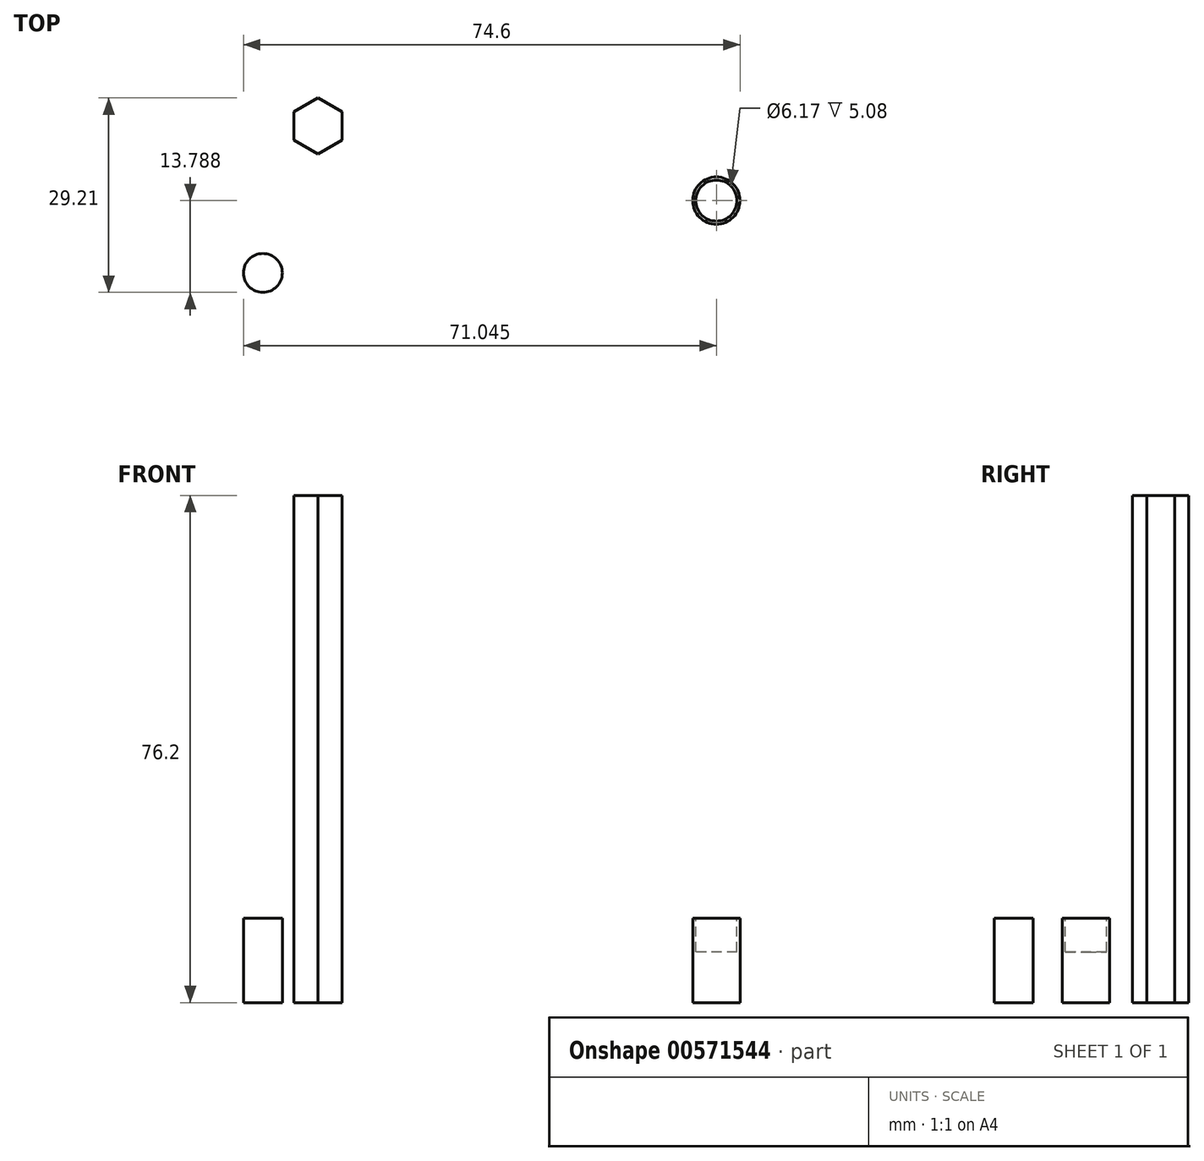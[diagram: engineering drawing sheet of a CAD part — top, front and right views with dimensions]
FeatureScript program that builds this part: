
annotation { "Feature Type Name" : "Feature", "Feature Type Description" : "" }
export const myFeature = defineFeature(function(context is Context, id is Id, definition is map)
    precondition{}
    {
        {
            var Q0;
            Q0=qCreatedBy(makeId("Top.planeOp"),FACE);
            var sketch = newSketch(context, id + "F0", { "sketchPlane" : qUnion([Q0])});
            skCircle(sketch, "E0.cCircle", {"center": v(-34.06, 44.97) * mm, "radius": 3.64 * mm, "construction": true});
            skLineSegment(sketch, "E0.0", {"start": v(-30.42, 47.07) * mm, "end": v(-30.42, 42.87) * mm});
            skLineSegment(sketch, "E0.1", {"start": v(-30.42, 42.87) * mm, "end": v(-34.06, 40.76) * mm});
            skLineSegment(sketch, "E0.2", {"start": v(-34.06, 40.76) * mm, "end": v(-37.7, 42.87) * mm});
            skLineSegment(sketch, "E0.3", {"start": v(-37.7, 42.87) * mm, "end": v(-37.7, 47.07) * mm});
            skLineSegment(sketch, "E0.4", {"start": v(-37.7, 47.07) * mm, "end": v(-34.06, 49.17) * mm});
            skLineSegment(sketch, "E0.5", {"start": v(-34.06, 49.17) * mm, "end": v(-30.42, 47.07) * mm});
            skPoint(sketch, "E0.0.midPoint", {"position": v(-30.42, 44.97) * mm});
            skSolve(sketch);
        }
        {
            var Q0;
            Q0=makeQuery(id+"F0.imprint","IMPRINT",FACE,{"disambiguationData":[TD([[makeQuery(id+"F0.imprint","IMPRINT",EDGE,{"derivedFrom":sQuery(id+"F0.wireOp",EDGE,"E0.0")}),-1.0]])]});
            extrude(context, id + "F1", {"entities" : qUnion([Q0]), "depth" : 76.2 * mm, "offsetDistance" : 25.4 * mm});
        }
        {
            var Q0;
            Q0=qCreatedBy(makeId("Top.planeOp"),FACE);
            var sketch = newSketch(context, id + "F2", { "sketchPlane" : qUnion([Q0])});
            skCircle(sketch, "E1", {"center": v(25.79, 33.75) * mm, "radius": 3.56 * mm});
            skSolve(sketch);
        }
        {
            var Q0;
            Q0 = qSketchRegion(id + "F2", true);
            extrude(context, id + "F3", {"entities" : qUnion([Q0]), "depth" : 12.7 * mm, "offsetDistance" : 25.4 * mm});
        }
        {
            var Q0;
            Q0=makeQuery(id+"F3.opExtrude","CAP_FACE",FACE,{"disambiguationData":[OSD([sQuery(id+"F2.wireOp",EDGE,"E1")])],"isStart":false});
            var sketch = newSketch(context, id + "F4", { "sketchPlane" : qUnion([Q0])});
            skCircle(sketch, "E2", {"center": v(25.79, 33.75) * mm, "radius": 3.09 * mm});
            skSolve(sketch);
        }
        {
            var Q0;
            Q0=makeQuery(id+"F4.imprint","IMPRINT",FACE,{"disambiguationData":[TD([[makeQuery(id+"F4.imprint","IMPRINT",EDGE,{"derivedFrom":sQuery(id+"F4.wireOp",EDGE,"E2")}),1.0]])]});
            extrude(context, id + "F5", {"entities" : qUnion([Q0]), "operationType" : NewBodyOperationType.REMOVE, "oppositeDirection" : true, "depth" : 5.08 * mm, "offsetDistance" : 25.4 * mm});
        }
        {
            var Q0;
            Q0=qCreatedBy(makeId("Top.planeOp"),FACE);
            var sketch = newSketch(context, id + "F6", { "sketchPlane" : qUnion([Q0])});
            skCircle(sketch, "E3", {"center": v(-42.34, 22.88) * mm, "radius": 2.92 * mm});
            skSolve(sketch);
        }
        {
            var Q0;
            Q0=makeQuery(id+"F6.imprint","IMPRINT",FACE,{"disambiguationData":[TD([[makeQuery(id+"F6.imprint","IMPRINT",EDGE,{"derivedFrom":sQuery(id+"F6.wireOp",EDGE,"E3")}),1.0]])]});
            extrude(context, id + "F7", {"entities" : qUnion([Q0]), "depth" : 12.7 * mm, "offsetDistance" : 25.4 * mm});
        }
    });
